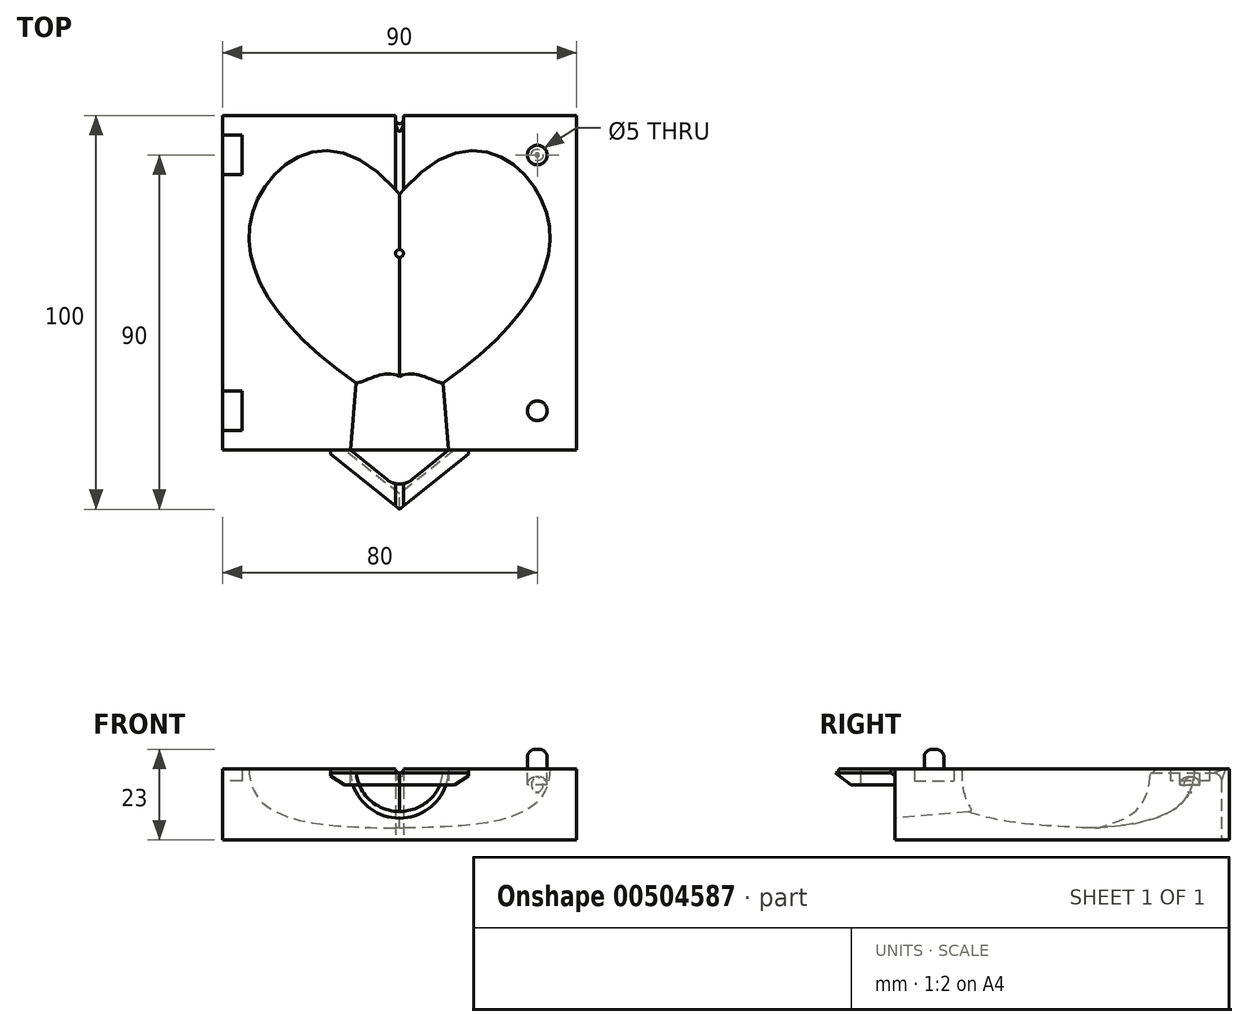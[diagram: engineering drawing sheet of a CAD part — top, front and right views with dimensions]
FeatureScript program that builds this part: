
annotation { "Feature Type Name" : "Feature", "Feature Type Description" : "" }
export const myFeature = defineFeature(function(context is Context, id is Id, definition is map)
    precondition{}
    {
        {
            var Q0;
            Q0=qCreatedBy(makeId("Top.planeOp"),FACE);
            var sketch = newSketch(context, id + "F0", { "sketchPlane" : qUnion([Q0])});
            skCircle(sketch, "E0", {"center": v(0, -35) * mm, "radius": 1 * mm});
            skSolve(sketch);
        }
        {
            var Q0;
            Q0=qCreatedBy(makeId("Front.planeOp"),FACE);
            var sketch = newSketch(context, id + "F1", { "sketchPlane" : qUnion([Q0])});
            skCircle(sketch, "E1", {"center": v(0, 15) * mm, "radius": 1 * mm});
            skSolve(sketch);
        }
        {
            var Q0;
            Q0=qCreatedBy(makeId("Top.planeOp"),FACE);
            cPlane(context, id + "F2", {"entities" : qUnion([Q0]), "cplaneType" : CPlaneType.OFFSET, "offset" : 15 * mm, "width" : 150 * mm, "height" : 150 * mm});
        }
        {
            var Q0;
            Q0=qCreatedBy(id+"F2.planeOp",FACE);
            var sketch = newSketch(context, id + "F3", { "sketchPlane" : qUnion([Q0])});
            skFitSpline(sketch, "E2.MirrorCS", {"points": [v(0, -20) * mm, v(-37, -23.7) * mm, v(0, -75) * mm], "startDerivative": vector(-115.24, 141.28) * mm, "endDerivative": vector(150.55, -88.28) * mm});
            skLineSegment(sketch, "E3", {"start": v(0, -20) * mm, "end": v(0, -75) * mm, "construction": true});
            skFitSpline(sketch, "E4.MirrorCS", {"points": [v(0, -20) * mm, v(37, -23.7) * mm, v(0, -75) * mm], "startDerivative": vector(115.24, 141.28) * mm, "endDerivative": vector(-150.55, -88.28) * mm});
            skSolve(sketch);
        }
        {
            var Q0;
            Q0=makeQuery(id+"F0.imprint","IMPRINT",FACE,{"disambiguationData":[TD([[makeQuery(id+"F0.imprint","IMPRINT",EDGE,{"derivedFrom":sQuery(id+"F0.wireOp",EDGE,"E0")}),1.0]])]});
            var Q1;
            Q1=makeQuery(id+"F3.imprint","IMPRINT",FACE,{"disambiguationData":[TD([[makeQuery(id+"F3.imprint","IMPRINT",EDGE,{"derivedFrom":sQuery(id+"F3.wireOp",EDGE,"E2.MirrorCS")}),1.0]])]});
            loft(context, id + "F4", {"startCondition" : LoftEndDerivativeType.NORMAL_TO_PROFILE, "startMagnitude" : 0, "endCondition" : LoftEndDerivativeType.NORMAL_TO_PROFILE, "endMagnitude" : 2.2, "sheetProfilesArray" : [{ "sheetProfileEntities" : qUnion([Q0]) }, { "sheetProfileEntities" : qUnion([Q1]) }]});
        }
        {
            var Q0;
            Q0=qSketchRegion(id+"F1",true);
            extrude(context, id + "F5", {"entities" : qUnion([Q0]), "operationType" : NewBodyOperationType.ADD, "depth" : 100 * mm, "offsetDistance" : 25 * mm});
        }
        {
            var Q0;
            Q0=qCreatedBy(id+"F2.planeOp",FACE);
            var sketch = newSketch(context, id + "F6", { "sketchPlane" : qUnion([Q0])});
            skLineSegment(sketch, "E5.bottom", {"start": v(45, 0) * mm, "end": v(-45, 0) * mm});
            skLineSegment(sketch, "E5.top", {"start": v(45, -85) * mm, "end": v(-45, -85) * mm});
            skLineSegment(sketch, "E5.left", {"start": v(45, 0) * mm, "end": v(45, -85) * mm});
            skLineSegment(sketch, "E5.right", {"start": v(-45, 0) * mm, "end": v(-45, -85) * mm});
            skPoint(sketch, "E5.middle", {"position": v(0, -42.5) * mm});
            skSolve(sketch);
        }
        {
            var Q0;
            Q0=makeQuery(id+"F6.imprint","IMPRINT",FACE,{"disambiguationData":[TD([[makeQuery(id+"F6.imprint","IMPRINT",EDGE,{"derivedFrom":sQuery(id+"F6.wireOp",EDGE,"E5.bottom")}),1.0]])]});
            extrude(context, id + "F7", {"entities" : qUnion([Q0]), "oppositeDirection" : true, "depth" : 18 * mm, "offsetDistance" : 25 * mm});
        }
        {
            var Q0;
            Q0=makeQuery(id+"F4.opLoft","SWEPT_BODY",BODY,{"disambiguationData":[OSD([makeQuery(id+"F0.imprint","IMPRINT",FACE,{"disambiguationData":[TD([[makeQuery(id+"F0.imprint","IMPRINT",EDGE,{"derivedFrom":sQuery(id+"F0.wireOp",EDGE,"E0")}),1.0]])]}),makeQuery(id+"F3.imprint","IMPRINT",FACE,{"disambiguationData":[TD([[makeQuery(id+"F3.imprint","IMPRINT",EDGE,{"derivedFrom":sQuery(id+"F3.wireOp",EDGE,"E2.MirrorCS")}),1.0]])]})])]});
            var Q1;
            Q1=makeQuery(id+"F7.opExtrude","SWEPT_BODY",BODY,{"disambiguationData":[OSD([sQuery(id+"F6.wireOp",EDGE,"E5.bottom"),sQuery(id+"F6.wireOp",EDGE,"E5.top"),sQuery(id+"F6.wireOp",EDGE,"E5.left"),sQuery(id+"F6.wireOp",EDGE,"E5.right")])]});
            booleanBodies(context, id + "F8", {"operationType" : BooleanOperationType.SUBTRACTION, "tools" : qUnion([Q0]), "targets" : qUnion([Q1])});
        }
        {
            var Q0;
            Q0=makeQuery(id+"F7.opExtrude","SWEPT_FACE",FACE,{"disambiguationData":[OSD([sQuery(id+"F6.wireOp",EDGE,"E5.top")])]});
            var sketch = newSketch(context, id + "F9", { "sketchPlane" : qUnion([Q0])});
            skCircle(sketch, "E6", {"center": v(0, 15) * mm, "radius": 12.5 * mm});
            skSolve(sketch);
        }
        {
            var Q0;
            {var subQ1=makeQuery(id+"F5.opExtrude","SWEPT_FACE",FACE,{"disambiguationData":[OSD([sQuery(id+"F1.wireOp",EDGE,"E1")])]});var subQ4=sQuery(id+"F6.wireOp",EDGE,"E5.top");var subQ6=makeQuery(id+"F7.opExtrude","SWEPT_FACE",FACE,{"disambiguationData":[OSD([subQ4])]});var subQ12=makeQuery(id+"F8.opBoolean","INTERSECT",EDGE,{"derivedFrom":[subQ1,subQ6]});Q0=makeQuery(id+"F9.imprint","IMPRINT",FACE,{"disambiguationData":[TD([[makeQuery(id+"F9.imprint","IMPRINT",EDGE,{"derivedFrom":subQ12}),1.0]])]});}
            var Q1;
            {var subQ1=makeQuery(id+"F5.opExtrude","SWEPT_FACE",FACE,{"disambiguationData":[OSD([sQuery(id+"F1.wireOp",EDGE,"E1")])]});var subQ4=sQuery(id+"F6.wireOp",EDGE,"E5.top");var subQ6=makeQuery(id+"F7.opExtrude","SWEPT_FACE",FACE,{"disambiguationData":[OSD([subQ4])]});var subQ12=makeQuery(id+"F8.opBoolean","INTERSECT",EDGE,{"derivedFrom":[subQ1,subQ6]});Q1=makeQuery(id+"F9.imprint","IMPRINT",FACE,{"disambiguationData":[TD([[makeQuery(id+"F9.imprint","IMPRINT",EDGE,{"derivedFrom":subQ12}),-1.0]])]});}
            extrude(context, id + "F10", {"entities" : qUnion([Q0, Q1]), "operationType" : NewBodyOperationType.REMOVE, "oppositeDirection" : true, "depth" : 25 * mm, "offsetDistance" : 25 * mm, "hasDraft" : true, "draftAngle" : 5 * degree, "draftPullDirection" : true});
        }
        {
            var Q0;
            {var subQ0=sQuery(id+"F6.wireOp",EDGE,"E5.top");var subQ3=sQuery(id+"F6.wireOp",EDGE,"E5.bottom");var subQ11=sQuery(id+"F6.wireOp",EDGE,"E5.right");var subQ12=sQuery(id+"F6.wireOp",EDGE,"E5.left");var subQ13=makeQuery(id+"F7.opExtrude","CAP_FACE",FACE,{"disambiguationData":[OSD([subQ3,subQ0,subQ12,subQ11])],"isStart":true});Q0=makeQuery(id+"F862zG6MbWRnyuZ_5.boolean.opBoolean","MERGE",FACE,{"derivedFrom":[makeQuery(id+"F8.opBoolean","SPLIT",FACE,{"disambiguationData":[TD([makeQuery(id+"F7.opExtrude","SWEPT_FACE",FACE,{"disambiguationData":[OSD([subQ12])]})])],"derivedFrom":subQ13}),makeQuery(id+"F8.opBoolean","SPLIT",FACE,{"disambiguationData":[TD([makeQuery(id+"F7.opExtrude","SWEPT_FACE",FACE,{"disambiguationData":[OSD([subQ11])]})])],"derivedFrom":subQ13}),makeQuery(id+"F862zG6MbWRnyuZ_5.opExtrude","SWEPT_FACE",FACE,{"disambiguationData":[OSD([sQuery(id+"F4vjdrcfKm0Qrqr_5.wireOp",EDGE,"fZ2rt3hO-zfMS-4lAD-JQZU-X3K6kq08anMB")])]})]});}
            var sketch = newSketch(context, id + "F11", { "sketchPlane" : qUnion([Q0])});
            skLineSegment(sketch, "E7.bottom", {"start": v(45, -88) * mm, "end": v(17.5, -88) * mm});
            skLineSegment(sketch, "E7.top", {"start": v(45, -85) * mm, "end": v(17.5, -85) * mm});
            skLineSegment(sketch, "E7.left", {"start": v(45, -88) * mm, "end": v(45, -85) * mm});
            skLineSegment(sketch, "E7.right", {"start": v(17.5, -88) * mm, "end": v(17.5, -85) * mm});
            skLineSegment(sketch, "E8.MirrorCS", {"start": v(-45, -88) * mm, "end": v(-45, -85) * mm});
            skLineSegment(sketch, "E9.MirrorCS", {"start": v(-17.5, -88) * mm, "end": v(-17.5, -85) * mm});
            skLineSegment(sketch, "E10.MirrorCS", {"start": v(-45, -88) * mm, "end": v(-17.5, -88) * mm});
            skLineSegment(sketch, "E11.MirrorCS", {"start": v(-45, -85) * mm, "end": v(-17.5, -85) * mm});
            skSolve(sketch);
        }
        {
            var Q0;
            Q0=makeQuery(id+"F11.imprint","IMPRINT",FACE,{"disambiguationData":[TD([[makeQuery(id+"F11.imprint","IMPRINT",EDGE,{"derivedFrom":sQuery(id+"F11.wireOp",EDGE,"E7.bottom")}),1.0]])]});
            var Q1;
            Q1=makeQuery(id+"F11.imprint","IMPRINT",FACE,{"disambiguationData":[TD([[makeQuery(id+"F11.imprint","IMPRINT",EDGE,{"derivedFrom":sQuery(id+"F11.wireOp",EDGE,"E8.MirrorCS")}),-1.0]])]});
            var Q2;
            {var subQ0=sQuery(id+"F11.wireOp",EDGE,"E9.MirrorCS");Q2=makeQuery(id+"F11.imprint","IMPRINT",FACE,{"disambiguationData":[TD([[makeQuery(id+"F11.imprint","IMPRINT",EDGE,{"derivedFrom":subQ0}),1.0]])]});}
            extrude(context, id + "F12", {"entities" : qUnion([Q0, Q1, Q2]), "operationType" : NewBodyOperationType.REMOVE, "oppositeDirection" : true, "depth" : 25 * mm, "offsetDistance" : 25 * mm});
        }
        {
            var Q0;
            {var subQ15=sQuery(id+"F11.wireOp",EDGE,"E7.top");Q0=makeQuery(id+"F11.imprint","IMPRINT",FACE,{"disambiguationData":[TD([[makeQuery(id+"F11.imprint","IMPRINT",EDGE,{"derivedFrom":subQ15}),-1.0]])]});}
            var sketch = newSketch(context, id + "F13", { "sketchPlane" : qUnion([Q0])});
            skCircle(sketch, "E12", {"center": v(35, -75) * mm, "radius": 2.5 * mm});
            skCircle(sketch, "E13", {"center": v(35, -10) * mm, "radius": 2.5 * mm});
            skCircle(sketch, "E14.MirrorC", {"center": v(-35, -75) * mm, "radius": 2.5 * mm});
            skCircle(sketch, "E15.MirrorC", {"center": v(-35, -10) * mm, "radius": 2.5 * mm});
            skSolve(sketch);
        }
        {
            var Q0;
            Q0=makeQuery(id+"F13.imprint","IMPRINT",FACE,{"disambiguationData":[TD([[makeQuery(id+"F13.imprint","IMPRINT",EDGE,{"derivedFrom":sQuery(id+"F13.wireOp",EDGE,"E12")}),1.0]])]});
            var Q1;
            Q1=makeQuery(id+"F13.imprint","IMPRINT",FACE,{"disambiguationData":[TD([[makeQuery(id+"F13.imprint","IMPRINT",EDGE,{"derivedFrom":sQuery(id+"F13.wireOp",EDGE,"E15.MirrorC")}),-1.0]])]});
            extrude(context, id + "F14", {"entities" : qUnion([Q0, Q1]), "operationType" : NewBodyOperationType.ADD, "depth" : 5 * mm, "offsetDistance" : 25 * mm});
        }
        {
            var Q0;
            Q0=makeQuery(id+"F13.imprint","IMPRINT",FACE,{"disambiguationData":[TD([[makeQuery(id+"F13.imprint","IMPRINT",EDGE,{"derivedFrom":sQuery(id+"F13.wireOp",EDGE,"E14.MirrorC")}),-1.0]])]});
            var Q1;
            Q1=makeQuery(id+"F13.imprint","IMPRINT",FACE,{"disambiguationData":[TD([[makeQuery(id+"F13.imprint","IMPRINT",EDGE,{"derivedFrom":sQuery(id+"F13.wireOp",EDGE,"E13")}),1.0]])]});
            extrude(context, id + "F15", {"entities" : qUnion([Q0, Q1]), "operationType" : NewBodyOperationType.REMOVE, "oppositeDirection" : true, "depth" : 6 * mm, "offsetDistance" : 25 * mm});
        }
        {
            var Q0;
            Q0=makeQuery(id+"F14.opExtrude","CAP_FACE",FACE,{"disambiguationData":[OSD([sQuery(id+"F13.wireOp",EDGE,"E12")])],"isStart":false});
            var Q1;
            Q1=makeQuery(id+"F14.opExtrude","CAP_FACE",FACE,{"disambiguationData":[OSD([sQuery(id+"F13.wireOp",EDGE,"E15.MirrorC")])],"isStart":false});
            var Q2;
            Q2=makeQuery(id+"F15.boolean.opBoolean","COPY",EDGE,{"derivedFrom":makeQuery(id+"F15.opExtrude","CAP_EDGE",EDGE,{"disambiguationData":[OSD([sQuery(id+"F13.wireOp",EDGE,"E14.MirrorC")])],"isStart":false})});
            var Q3;
            Q3=makeQuery(id+"F15.boolean.opBoolean","COPY",FACE,{"derivedFrom":makeQuery(id+"F15.opExtrude","CAP_FACE",FACE,{"disambiguationData":[OSD([sQuery(id+"F13.wireOp",EDGE,"E13")])],"isStart":false})});
            fillet(context, id + "F16", {"entities" : qUnion([Q0, Q1, Q2, Q3]), "radius" : 2 * mm, "tangentPropagation" : true, "allowEdgeOverflow" : false});
        }
        {
            var Q0;
            Q0=makeQuery(id+"F7.opExtrude","SWEPT_FACE",FACE,{"disambiguationData":[OSD([sQuery(id+"F6.wireOp",EDGE,"E5.bottom")])]});
            var sketch = newSketch(context, id + "F17", { "sketchPlane" : qUnion([Q0])});
            skLineSegment(sketch, "E16.bottom", {"start": v(-1, 15) * mm, "end": v(1, 15) * mm});
            skLineSegment(sketch, "E16.top", {"start": v(-1, -3) * mm, "end": v(1, -3) * mm});
            skLineSegment(sketch, "E16.left", {"start": v(-1, 15) * mm, "end": v(-1, -3) * mm});
            skLineSegment(sketch, "E16.right", {"start": v(1, 15) * mm, "end": v(1, -3) * mm});
            skSolve(sketch);
        }
        {
            var Q0;
            Q0 = qSketchRegion(id + "F17", true);
            extrude(context, id + "F18", {"entities" : qUnion([Q0]), "operationType" : NewBodyOperationType.REMOVE, "oppositeDirection" : true, "depth" : 2 * mm, "offsetDistance" : 25 * mm});
        }
        {
            var Q0;
            Q0=makeQuery(id+"F18.boolean.opBoolean","COPY",EDGE,{"derivedFrom":makeQuery(id+"F18.opExtrude","CAP_EDGE",EDGE,{"disambiguationData":[OSD([sQuery(id+"F17.wireOp",EDGE,"E16.left")])],"isStart":false})});
            var Q1;
            Q1=makeQuery(id+"F18.boolean.opBoolean","COPY",EDGE,{"derivedFrom":makeQuery(id+"F18.opExtrude","CAP_EDGE",EDGE,{"disambiguationData":[OSD([sQuery(id+"F17.wireOp",EDGE,"E16.right")])],"isStart":false})});
            fillet(context, id + "F19", {"entities" : qUnion([Q0, Q1]), "radius" : 1 * mm, "tangentPropagation" : true, "allowEdgeOverflow" : false});
        }
        {
            var Q0;
            {var subQ6=sQuery(id+"F6.wireOp",EDGE,"E5.bottom");Q0=makeQuery(id+"F19.opFillet","BLEND_EDGE",EDGE,{"blendedFrom":[makeQuery(id+"F18.boolean.opBoolean","COPY",EDGE,{"derivedFrom":makeQuery(id+"F18.opExtrude","CAP_EDGE",EDGE,{"disambiguationData":[OSD([sQuery(id+"F17.wireOp",EDGE,"E16.left")])],"isStart":false})}),makeQuery(id+"F8.opBoolean","COPY",FACE,{"disambiguationData":[TD([makeQuery(id+"F7.opExtrude","SWEPT_FACE",FACE,{"disambiguationData":[OSD([subQ6])]})])],"derivedFrom":makeQuery(id+"F5.opExtrude","SWEPT_FACE",FACE,{"disambiguationData":[OSD([sQuery(id+"F1.wireOp",EDGE,"E1")])]})})],"blendedInto":[makeQuery(id+"F8.opBoolean","COPY",FACE,{"disambiguationData":[TD([makeQuery(id+"F7.opExtrude","SWEPT_FACE",FACE,{"disambiguationData":[OSD([subQ6])]})])],"derivedFrom":makeQuery(id+"F5.opExtrude","SWEPT_FACE",FACE,{"disambiguationData":[OSD([sQuery(id+"F1.wireOp",EDGE,"E1")])]})})]});}
            var Q1;
            {var subQ6=sQuery(id+"F6.wireOp",EDGE,"E5.bottom");Q1=makeQuery(id+"F19.opFillet","BLEND_EDGE",EDGE,{"blendedFrom":[makeQuery(id+"F18.boolean.opBoolean","COPY",EDGE,{"derivedFrom":makeQuery(id+"F18.opExtrude","CAP_EDGE",EDGE,{"disambiguationData":[OSD([sQuery(id+"F17.wireOp",EDGE,"E16.right")])],"isStart":false})}),makeQuery(id+"F8.opBoolean","COPY",FACE,{"disambiguationData":[TD([makeQuery(id+"F7.opExtrude","SWEPT_FACE",FACE,{"disambiguationData":[OSD([subQ6])]})])],"derivedFrom":makeQuery(id+"F5.opExtrude","SWEPT_FACE",FACE,{"disambiguationData":[OSD([sQuery(id+"F1.wireOp",EDGE,"E1")])]})})],"blendedInto":[makeQuery(id+"F8.opBoolean","COPY",FACE,{"disambiguationData":[TD([makeQuery(id+"F7.opExtrude","SWEPT_FACE",FACE,{"disambiguationData":[OSD([subQ6])]})])],"derivedFrom":makeQuery(id+"F5.opExtrude","SWEPT_FACE",FACE,{"disambiguationData":[OSD([sQuery(id+"F1.wireOp",EDGE,"E1")])]})})]});}
            fillet(context, id + "F20", {"entities" : qUnion([Q0, Q1]), "radius" : 2 * mm, "tangentPropagation" : true, "allowEdgeOverflow" : false});
        }
        {
            var Q0;
            Q0=makeQuery(id+"F7.opExtrude","SWEPT_FACE",FACE,{"disambiguationData":[OSD([sQuery(id+"F6.wireOp",EDGE,"E5.right")])]});
            var sketch = newSketch(context, id + "F21", { "sketchPlane" : qUnion([Q0])});
            skLineSegment(sketch, "E17.bottom", {"start": v(80, 15) * mm, "end": v(70, 15) * mm});
            skLineSegment(sketch, "E17.top", {"start": v(80, 12) * mm, "end": v(70, 12) * mm});
            skLineSegment(sketch, "E17.left", {"start": v(80, 15) * mm, "end": v(80, 12) * mm});
            skLineSegment(sketch, "E17.right", {"start": v(70, 15) * mm, "end": v(70, 12) * mm});
            skLineSegment(sketch, "E18.bottom", {"start": v(5, 15) * mm, "end": v(15, 15) * mm});
            skLineSegment(sketch, "E18.top", {"start": v(5, 12) * mm, "end": v(15, 12) * mm});
            skLineSegment(sketch, "E18.left", {"start": v(5, 15) * mm, "end": v(5, 12) * mm});
            skLineSegment(sketch, "E18.right", {"start": v(15, 15) * mm, "end": v(15, 12) * mm});
            skSolve(sketch);
        }
        {
            var Q0;
            Q0=makeQuery(id+"F21.imprint","IMPRINT",FACE,{"disambiguationData":[TD([[makeQuery(id+"F21.imprint","IMPRINT",EDGE,{"derivedFrom":sQuery(id+"F21.wireOp",EDGE,"E17.bottom")}),-1.0]])]});
            var Q1;
            Q1=makeQuery(id+"F21.imprint","IMPRINT",FACE,{"disambiguationData":[TD([[makeQuery(id+"F21.imprint","IMPRINT",EDGE,{"derivedFrom":sQuery(id+"F21.wireOp",EDGE,"E18.bottom")}),-1.0]])]});
            extrude(context, id + "F22", {"entities" : qUnion([Q0, Q1]), "operationType" : NewBodyOperationType.REMOVE, "oppositeDirection" : true, "depth" : 5 * mm, "offsetDistance" : 25 * mm});
        }
        {
            var Q0;
            Q0=makeQuery(id+"F13.imprint","IMPRINT",FACE,{"disambiguationData":[TD([[makeQuery(id+"F13.imprint","IMPRINT",EDGE,{"derivedFrom":sQuery(id+"F13.wireOp",EDGE,"E12")}),-1.0]])]});
            var sketch = newSketch(context, id + "F23", { "sketchPlane" : qUnion([Q0])});
            skLineSegment(sketch, "E19", {"start": v(17.5, -86) * mm, "end": v(0, -100) * mm});
            skLineSegment(sketch, "E20", {"start": v(0, -100) * mm, "end": v(0, -95) * mm});
            skLineSegment(sketch, "E21", {"start": v(0, -95) * mm, "end": v(12.5, -85) * mm});
            skLineSegment(sketch, "E22", {"start": v(12.5, -85) * mm, "end": v(12.5, -90) * mm});
            skLineSegment(sketch, "E23.MirrorCS", {"start": v(-12.5, -85) * mm, "end": v(-12.5, -90) * mm});
            skLineSegment(sketch, "E24.MirrorCS", {"start": v(-17.5, -86) * mm, "end": v(0, -100) * mm});
            skLineSegment(sketch, "E25.MirrorCS", {"start": v(0, -95) * mm, "end": v(-12.5, -85) * mm});
            skLineSegment(sketch, "E26.top", {"start": v(12.5, -85) * mm, "end": v(17.5, -85) * mm});
            skLineSegment(sketch, "E26.left", {"start": v(12.5, -90) * mm, "end": v(12.5, -85) * mm});
            skLineSegment(sketch, "E27.MirrorCS", {"start": v(-12.5, -85) * mm, "end": v(-17.5, -85) * mm});
            skLineSegment(sketch, "E28.MirrorCS", {"start": v(-17.5, -86) * mm, "end": v(-17.5, -85) * mm});
            skLineSegment(sketch, "E29.MirrorCS", {"start": v(-12.5, -90) * mm, "end": v(0, -100) * mm});
            skLineSegment(sketch, "E30.MirrorCS", {"start": v(-12.5, -90) * mm, "end": v(-12.5, -85) * mm});
            skLineSegment(sketch, "E31", {"start": v(17.5, -86) * mm, "end": v(17.5, -85) * mm});
            skSolve(sketch);
        }
        {
            var Q0;
            Q0=makeQuery(id+"F23.imprint","IMPRINT",FACE,{"disambiguationData":[TD([[makeQuery(id+"F23.imprint","IMPRINT",EDGE,{"derivedFrom":sQuery(id+"F23.wireOp",EDGE,"E23.MirrorCS")}),1.0]])]});
            var Q1;
            Q1=makeQuery(id+"F23.imprint","IMPRINT",FACE,{"disambiguationData":[TD([[makeQuery(id+"F23.imprint","IMPRINT",EDGE,{"derivedFrom":sQuery(id+"F23.wireOp",EDGE,"E19")}),-1.0]])]});
            var Q2;
            Q2=makeQuery(id+"F23.imprint","IMPRINT",FACE,{"disambiguationData":[TD([[makeQuery(id+"F23.imprint","IMPRINT",EDGE,{"derivedFrom":sQuery(id+"F23.wireOp",EDGE,"E26.bottom")}),1.0]])]});
            var Q3;
            Q3=makeQuery(id+"F23.imprint","IMPRINT",FACE,{"disambiguationData":[TD([[makeQuery(id+"F23.imprint","IMPRINT",EDGE,{"derivedFrom":sQuery(id+"F23.wireOp",EDGE,"E20")}),1.0]])]});
            var Q4;
            Q4=makeQuery(id+"F23.imprint","IMPRINT",FACE,{"disambiguationData":[TD([[makeQuery(id+"F23.imprint","IMPRINT",EDGE,{"derivedFrom":sQuery(id+"F23.wireOp",EDGE,"E27.MirrorCS")}),1.0]])]});
            extrude(context, id + "F24", {"entities" : qUnion([Q0, Q1, Q2, Q3, Q4]), "oppositeDirection" : true, "depth" : 4 * mm, "offsetDistance" : 25 * mm});
        }
        {
            var Q0;
            Q0=makeQuery(id+"F24.opExtrude","CAP_EDGE",EDGE,{"disambiguationData":[OSD([sQuery(id+"F23.wireOp",EDGE,"E24.MirrorCS"),sQuery(id+"F23.wireOp",EDGE,"E29.MirrorCS")])],"isStart":false});
            var Q1;
            Q1=makeQuery(id+"F24.opExtrude","CAP_EDGE",EDGE,{"disambiguationData":[OSD([sQuery(id+"F23.wireOp",EDGE,"E19")])],"isStart":false});
            chamfer(context, id + "F25", {"entities" : qUnion([Q0, Q1]), "width" : 3 * mm, "tangentPropagation" : true});
        }
        {
            var Q0;
            Q0=makeQuery(id+"F7.opExtrude","SWEPT_FACE",FACE,{"disambiguationData":[OSD([sQuery(id+"F6.wireOp",EDGE,"E5.top")])]});
            var sketch = newSketch(context, id + "F26", { "sketchPlane" : qUnion([Q0])});
            skCircle(sketch, "E32", {"center": v(0, 15) * mm, "radius": 1 * mm});
            skSolve(sketch);
        }
        {
            var Q0;
            Q0 = qSketchRegion(id + "F26", true);
            extrude(context, id + "F27", {"entities" : qUnion([Q0]), "operationType" : NewBodyOperationType.REMOVE, "depth" : 25 * mm, "offsetDistance" : 25 * mm});
        }
        {
            var Q0;
            Q0=makeQuery(id+"F24.opExtrude","SWEPT_EDGE",EDGE,{"disambiguationData":[OSD([sQuery(id+"F23.wireOp",EDGE,"E21"),sQuery(id+"F23.wireOp",EDGE,"E20"),sQuery(id+"F23.wireOp",EDGE,"E25.MirrorCS")])]});
            var Q1;
            Q1=makeQuery(id+"F24.opExtrude","SWEPT_EDGE",EDGE,{"disambiguationData":[OSD([sQuery(id+"F23.wireOp",EDGE,"E19"),sQuery(id+"F23.wireOp",EDGE,"E20"),sQuery(id+"F23.wireOp",EDGE,"E29.MirrorCS")])]});
            fillet(context, id + "F28", {"entities" : qUnion([Q0, Q1]), "radius" : 5 * mm, "tangentPropagation" : true, "allowEdgeOverflow" : false});
        }
    });
